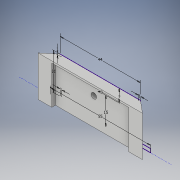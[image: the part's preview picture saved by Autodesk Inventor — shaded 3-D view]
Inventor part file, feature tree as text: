
AUTODESK INVENTOR PART (.ipt)
format: ipt  version: 2019 (Build 230136000, 136)  size: 240,128 bytes
history: native  units: mm
features: extrude x2, sketch x1, draft x1, direct_edit x1, move_body x1
ambient origin geometry x8: Origin, YZ Plane, XZ Plane, XY Plane, X Axis, Y Axis, Z Axis, Center Point
bodies: Solid1 (feature_tree)
feature tree (6):
  sketch  "Sketch1"  dims[d0=3.0mm d1=7.0mm d2=44.0mm d3=20.0mm d4=15.0mm d5=1.0mm d8=1.0mm d9=1.0mm d10=55.0mm d11=5.5mm d12=0.0mm d13=3.5mm d14=0.0mm d19=8.726646mm d23=0.0mm d24=0.0mm d25=2.0mm]
  extrude  "Extrusion1"  Depth=2.0mm
  extrude  "Extrusion2"  Depth=2.0mm
  draft  "FaceDraft1"
  direct_edit  "Direct Edit1"
  move_body  "Move1"
